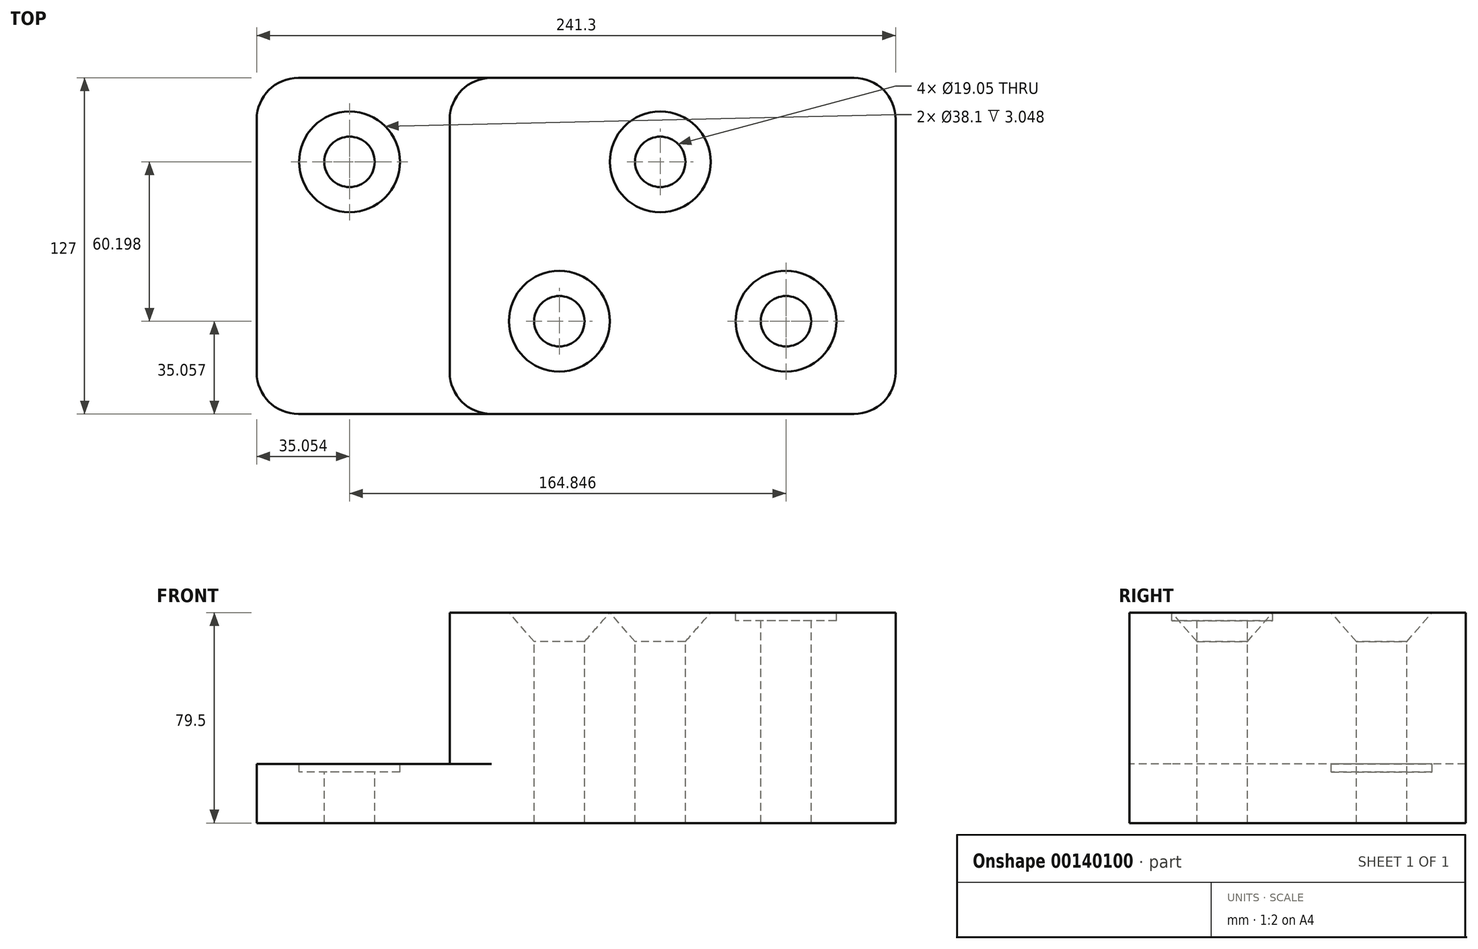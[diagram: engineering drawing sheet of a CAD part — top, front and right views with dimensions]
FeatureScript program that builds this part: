
annotation { "Feature Type Name" : "Feature", "Feature Type Description" : "" }
export const myFeature = defineFeature(function(context is Context, id is Id, definition is map)
    precondition{}
    {
        {
            var Q0;
            Q0=qCreatedBy(makeId("Top.planeOp"),FACE);
            var sketch = newSketch(context, id + "F0", { "sketchPlane" : qUnion([Q0])});
            skLineSegment(sketch, "E0.bottom", {"start": v(0, 59.8) * mm, "end": v(168.4, 59.8) * mm});
            skLineSegment(sketch, "E0.top", {"start": v(0, -67.2) * mm, "end": v(168.4, -67.2) * mm});
            skLineSegment(sketch, "E0.left", {"start": v(0, 59.8) * mm, "end": v(0, -67.2) * mm});
            skLineSegment(sketch, "E0.right", {"start": v(168.4, 59.8) * mm, "end": v(168.4, -67.2) * mm});
            skLineSegment(sketch, "E1.bottom", {"start": v(0, 59.8) * mm, "end": v(-72.9, 59.8) * mm});
            skLineSegment(sketch, "E1.top", {"start": v(0, -67.2) * mm, "end": v(-72.9, -67.2) * mm});
            skLineSegment(sketch, "E1.right", {"start": v(-72.9, 59.8) * mm, "end": v(-72.9, -67.2) * mm});
            skSolve(sketch);
        }
        {
            var Q0;
            Q0=makeQuery(id+"F0.imprint","IMPRINT",FACE,{"disambiguationData":[TD([[makeQuery(id+"F0.imprint","IMPRINT",EDGE,{"derivedFrom":sQuery(id+"F0.wireOp",EDGE,"E1.bottom")}),1.0]])]});
            var Q1;
            Q1=makeQuery(id+"F0.imprint","IMPRINT",FACE,{"disambiguationData":[TD([[makeQuery(id+"F0.imprint","IMPRINT",EDGE,{"derivedFrom":sQuery(id+"F0.wireOp",EDGE,"E0.bottom")}),-1.0]])]});
            extrude(context, id + "F1", {"entities" : qUnion([Q0, Q1]), "depth" : 22.35 * mm});
        }
        {
            var Q0;
            Q0=makeQuery(id+"F0.imprint","IMPRINT",FACE,{"disambiguationData":[TD([[makeQuery(id+"F0.imprint","IMPRINT",EDGE,{"derivedFrom":sQuery(id+"F0.wireOp",EDGE,"E0.bottom")}),-1.0]])]});
            extrude(context, id + "F2", {"entities" : qUnion([Q0]), "operationType" : NewBodyOperationType.ADD, "depth" : 79.5 * mm});
        }
        {
            var Q0;
            Q0=makeQuery(id+"F2.opExtrude","CAP_FACE",FACE,{"disambiguationData":[OSD([sQuery(id+"F0.wireOp",EDGE,"E0.bottom"),sQuery(id+"F0.wireOp",EDGE,"E0.top"),sQuery(id+"F0.wireOp",EDGE,"E0.right"),sQuery(id+"F0.wireOp",EDGE,"E0.left")])],"isStart":false});
            var sketch = newSketch(context, id + "F3", { "sketchPlane" : qUnion([Q0])});
            skCircle(sketch, "E2", {"center": v(127, -32.15) * mm, "radius": 9.53 * mm});
            skCircle(sketch, "E3", {"center": v(127, -32.15) * mm, "radius": 19.05 * mm});
            skSolve(sketch);
        }
        {
            var Q0;
            Q0=makeQuery(id+"F3.imprint","IMPRINT",FACE,{"disambiguationData":[TD([[makeQuery(id+"F3.imprint","IMPRINT",EDGE,{"derivedFrom":sQuery(id+"F3.wireOp",EDGE,"E2")}),1.0]])]});
            var Q1;
            Q1=makeQuery(id+"F1.opExtrude","CAP_FACE",FACE,{"disambiguationData":[OSD([sQuery(id+"F0.wireOp",EDGE,"E0.bottom"),sQuery(id+"F0.wireOp",EDGE,"E0.top"),sQuery(id+"F0.wireOp",EDGE,"E0.right"),sQuery(id+"F0.wireOp",EDGE,"E1.bottom"),sQuery(id+"F0.wireOp",EDGE,"E1.top"),sQuery(id+"F0.wireOp",EDGE,"E1.right")])],"isStart":true});
            extrude(context, id + "F4", {"entities" : qUnion([Q0]), "operationType" : NewBodyOperationType.REMOVE, "endBound" : BoundingType.UP_TO_SURFACE, "oppositeDirection" : true, "endBoundEntityFace" : qUnion([Q1]), "depth" : 3.05 * mm});
        }
        {
            var Q0;
            Q0=makeQuery(id+"F3.imprint","IMPRINT",FACE,{"disambiguationData":[TD([[makeQuery(id+"F3.imprint","IMPRINT",EDGE,{"derivedFrom":sQuery(id+"F3.wireOp",EDGE,"E2")}),-1.0]])]});
            extrude(context, id + "F5", {"entities" : qUnion([Q0]), "operationType" : NewBodyOperationType.REMOVE, "oppositeDirection" : true, "depth" : 3.05 * mm});
        }
        {
            var Q0;
            Q0=makeQuery(id+"F3.imprint","IMPRINT",FACE,{"disambiguationData":[TD([[makeQuery(id+"F3.imprint","IMPRINT",EDGE,{"derivedFrom":sQuery(id+"F3.wireOp",EDGE,"E3")}),-1.0]])]});
            var sketch = newSketch(context, id + "F6", { "sketchPlane" : qUnion([Q0])});
            skCircle(sketch, "E4", {"center": v(41.4, -32.15) * mm, "radius": 9.53 * mm});
            skLineSegment(sketch, "E5", {"start": v(41.4, -32.15) * mm, "end": v(127.05, -32.15) * mm, "construction": true});
            skCircle(sketch, "E6", {"center": v(41.4, -32.15) * mm, "radius": 19.05 * mm});
            skCircle(sketch, "E7", {"center": v(79.5, 28.04) * mm, "radius": 9.53 * mm});
            skCircle(sketch, "E8", {"center": v(79.5, 28.04) * mm, "radius": 19.05 * mm});
            skSolve(sketch);
        }
        {
            var Q0;
            Q0=makeQuery(id+"F6.imprint","IMPRINT",FACE,{"disambiguationData":[TD([[makeQuery(id+"F6.imprint","IMPRINT",EDGE,{"derivedFrom":sQuery(id+"F6.wireOp",EDGE,"E7")}),1.0]])]});
            var Q1;
            Q1=makeQuery(id+"F6.imprint","IMPRINT",FACE,{"disambiguationData":[TD([[makeQuery(id+"F6.imprint","IMPRINT",EDGE,{"derivedFrom":sQuery(id+"F6.wireOp",EDGE,"E4")}),1.0]])]});
            extrude(context, id + "F7", {"entities" : qUnion([Q0, Q1]), "operationType" : NewBodyOperationType.REMOVE, "endBound" : BoundingType.THROUGH_ALL, "oppositeDirection" : true, "depth" : 25.4 * mm});
        }
        {
            var Q0;
            Q0=sQuery(id+"F6.wireOp",VERTEX,"E7.center");
            var Q1;
            Q1=makeQuery(id+"F1.opExtrude","SWEPT_BODY",BODY,{"disambiguationData":[OSD([sQuery(id+"F0.wireOp",EDGE,"E0.bottom"),sQuery(id+"F0.wireOp",EDGE,"E0.top"),sQuery(id+"F0.wireOp",EDGE,"E0.right"),sQuery(id+"F0.wireOp",EDGE,"E1.bottom"),sQuery(id+"F0.wireOp",EDGE,"E1.top"),sQuery(id+"F0.wireOp",EDGE,"E1.right")])]});
            hole(context, id + "F8", {"style" : HoleStyle.C_SINK, "endStyle" : HoleEndStyle.THROUGH, "holeDiameter" : 19.05 * mm, "cSinkDiameter" : 38.1 * mm, "cSinkAngle" : 82 * degree, "locations" : qUnion([Q0]), "scope" : qUnion([Q1]), "isTappedThrough" : true});
        }
        {
            var Q0;
            Q0=sQuery(id+"F6.wireOp",VERTEX,"E5.start");
            var Q1;
            Q1=makeQuery(id+"F1.opExtrude","SWEPT_BODY",BODY,{"disambiguationData":[OSD([sQuery(id+"F0.wireOp",EDGE,"E0.bottom"),sQuery(id+"F0.wireOp",EDGE,"E0.top"),sQuery(id+"F0.wireOp",EDGE,"E0.right"),sQuery(id+"F0.wireOp",EDGE,"E1.bottom"),sQuery(id+"F0.wireOp",EDGE,"E1.top"),sQuery(id+"F0.wireOp",EDGE,"E1.right")])]});
            hole(context, id + "F9", {"style" : HoleStyle.C_SINK, "endStyle" : HoleEndStyle.THROUGH, "holeDiameter" : 19.05 * mm, "cSinkDiameter" : 38.1 * mm, "cSinkAngle" : 82 * degree, "locations" : qUnion([Q0]), "scope" : qUnion([Q1]), "isTappedThrough" : true});
        }
        {
            var Q0;
            Q0=makeQuery(id+"F1.opExtrude","CAP_FACE",FACE,{"disambiguationData":[OSD([sQuery(id+"F0.wireOp",EDGE,"E0.bottom"),sQuery(id+"F0.wireOp",EDGE,"E0.top"),sQuery(id+"F0.wireOp",EDGE,"E0.right"),sQuery(id+"F0.wireOp",EDGE,"E1.bottom"),sQuery(id+"F0.wireOp",EDGE,"E1.top"),sQuery(id+"F0.wireOp",EDGE,"E1.right")])],"isStart":false});
            var sketch = newSketch(context, id + "F10", { "sketchPlane" : qUnion([Q0])});
            skCircle(sketch, "E9", {"center": v(-37.85, 28.04) * mm, "radius": 19.05 * mm});
            skCircle(sketch, "E10", {"center": v(-37.85, 28.04) * mm, "radius": 9.53 * mm});
            skSolve(sketch);
        }
        {
            var Q0;
            Q0=sQuery(id+"F10.wireOp",VERTEX,"E9.center");
            var Q1;
            Q1=makeQuery(id+"F1.opExtrude","SWEPT_BODY",BODY,{"disambiguationData":[OSD([sQuery(id+"F0.wireOp",EDGE,"E0.bottom"),sQuery(id+"F0.wireOp",EDGE,"E0.top"),sQuery(id+"F0.wireOp",EDGE,"E0.right"),sQuery(id+"F0.wireOp",EDGE,"E1.bottom"),sQuery(id+"F0.wireOp",EDGE,"E1.top"),sQuery(id+"F0.wireOp",EDGE,"E1.right")])]});
            hole(context, id + "F11", {"style" : HoleStyle.C_BORE, "endStyle" : HoleEndStyle.THROUGH, "holeDiameter" : 19.05 * mm, "cBoreDiameter" : 38.1 * mm, "cBoreDepth" : 3.05 * mm, "locations" : qUnion([Q0]), "scope" : qUnion([Q1]), "isTappedThrough" : true});
        }
        {
            var Q0;
            Q0=makeQuery(id+"F2.opExtrude","SWEPT_EDGE",EDGE,{"disambiguationData":[OSD([sQuery(id+"F0.wireOp",EDGE,"E0.top"),sQuery(id+"F0.wireOp",EDGE,"E1.top"),sQuery(id+"F0.wireOp",EDGE,"E0.left")])]});
            var Q1;
            Q1=makeQuery(id+"F1.opExtrude","SWEPT_EDGE",EDGE,{"disambiguationData":[OSD([sQuery(id+"F0.wireOp",EDGE,"E1.top"),sQuery(id+"F0.wireOp",EDGE,"E1.right")])]});
            var Q2;
            Q2=makeQuery(id+"F2.opExtrude","SWEPT_EDGE",EDGE,{"disambiguationData":[OSD([sQuery(id+"F0.wireOp",EDGE,"E0.bottom"),sQuery(id+"F0.wireOp",EDGE,"E1.bottom"),sQuery(id+"F0.wireOp",EDGE,"E0.left")])]});
            var Q3;
            Q3=makeQuery(id+"F1.opExtrude","SWEPT_EDGE",EDGE,{"disambiguationData":[OSD([sQuery(id+"F0.wireOp",EDGE,"E1.bottom"),sQuery(id+"F0.wireOp",EDGE,"E1.right")])]});
            var Q4;
            {var subQ0=sQuery(id+"F0.wireOp",EDGE,"E0.right");var subQ1=sQuery(id+"F0.wireOp",EDGE,"E0.bottom");Q4=makeQuery(id+"F2.boolean.opBoolean","MERGE",EDGE,{"derivedFrom":[makeQuery(id+"F1.opExtrude","SWEPT_EDGE",EDGE,{"disambiguationData":[OSD([subQ1,subQ0])]}),makeQuery(id+"F2.opExtrude","SWEPT_EDGE",EDGE,{"disambiguationData":[OSD([subQ1,subQ0])]})]});}
            var Q5;
            {var subQ0=sQuery(id+"F0.wireOp",EDGE,"E0.right");var subQ1=sQuery(id+"F0.wireOp",EDGE,"E0.top");Q5=makeQuery(id+"F2.boolean.opBoolean","MERGE",EDGE,{"derivedFrom":[makeQuery(id+"F1.opExtrude","SWEPT_EDGE",EDGE,{"disambiguationData":[OSD([subQ1,subQ0])]}),makeQuery(id+"F2.opExtrude","SWEPT_EDGE",EDGE,{"disambiguationData":[OSD([subQ1,subQ0])]})]});}
            fillet(context, id + "F12", {"entities" : qUnion([Q0, Q1, Q2, Q3, Q4, Q5]), "radius" : 15.75 * mm, "tangentPropagation" : true, "allowEdgeOverflow" : false});
        }
    });
